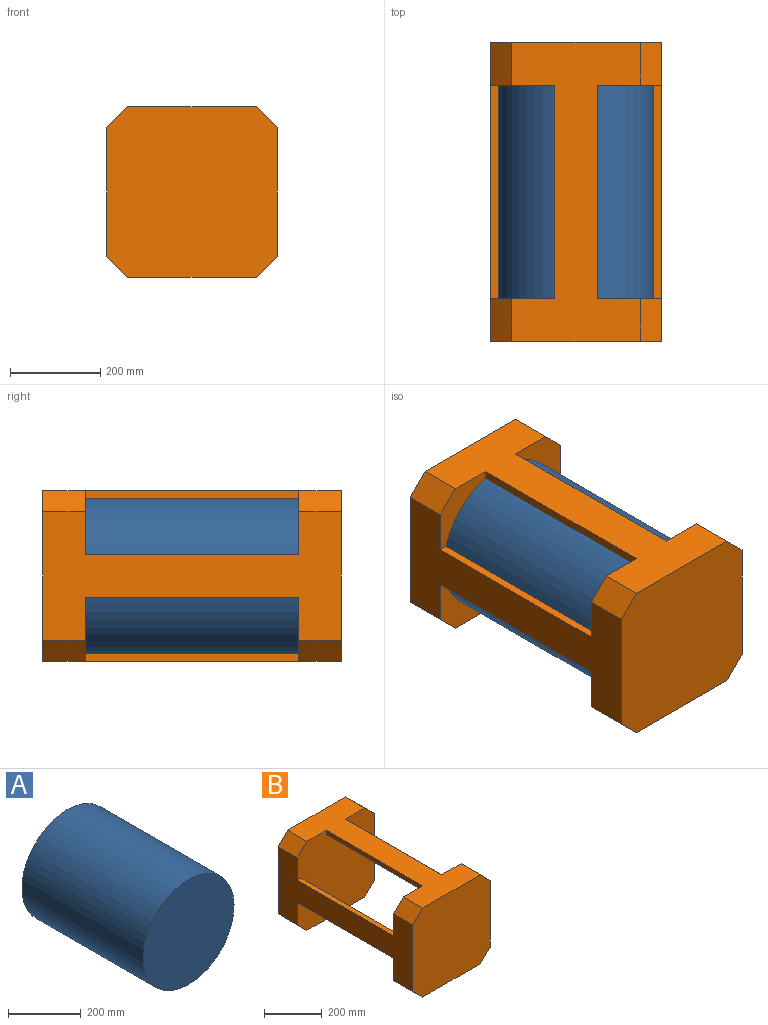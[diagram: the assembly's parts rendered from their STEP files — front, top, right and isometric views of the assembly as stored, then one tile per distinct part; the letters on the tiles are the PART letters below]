
ASSEMBLY  parts=2 mates=1
PART A: 3 faces, bbox 353.8x471.7x353.8 mm
  f0: cylinder r=176.89mm len=471.71mm, axis (0,-1,0), area 524287.1mm2, adj f1,f2
  f1: plane 353.79x353.79mm, normal (0,1,0), area 98303.8mm2, adj f0
  f2: plane 353.79x353.79mm, normal (0,-1,0), area 98303.8mm2, adj f0
PART B: 28 faces, bbox 377.4x660.4x377.4 mm
  f0: plane 377.37x377.37mm, normal (0,1,0), area 132708.8mm2, adj f1,f2,f3,f4,f5,f6,f7,f8
  f1: plane 660.4x283.03mm, normal (0,0,-1), area 97906.3mm2, adj f0,f2,f8,f9,f13,f14,f22,f23
  f2: plane 94.34x47.17mm, normal (0.71,0,-0.71), area 6293.7mm2, adj f0,f1,f3,f9
  f3: plane 660.4x283.03mm, normal (1,0,0), area 97906.3mm2, adj f0,f2,f4,f9,f19,f21,f22,f23
  f4: plane 94.34x47.17mm, normal (0.71,0,0.71), area 6293.7mm2, adj f0,f3,f5,f9
  f5: plane 660.4x283.03mm, normal (0,0,1), area 97906.3mm2, adj f0,f4,f6,f9,f10,f12,f22,f24
  f6: plane 94.34x47.17mm, normal (-0.71,0,0.71), area 6293.7mm2, adj f0,f5,f7,f9
  f7: plane 660.4x283.03mm, normal (-1,0,0), area 97906.3mm2, adj f0,f6,f8,f9,f17,f18,f22,f25
  f8: plane 94.34x47.17mm, normal (-0.71,0,-0.71), area 6293.7mm2, adj f0,f1,f7,f9
  f9: plane 377.37x377.37mm, normal (0,-1,0), area 137958.9mm2, adj f1,f2,f3,f4,f5,f6,f7,f8
  f10: plane 471.71x18.2mm, normal (-1,0,0), area 8584.4mm2, adj f0,f5,f11,f22
  f11: cylinder r=176.89mm len=471.71mm, axis (0,-1,0), area 45047.9mm2, adj f0,f10,f12,f22
  f12: plane 471.71x18.2mm, normal (1,0,0), area 8584.4mm2, adj f0,f5,f11,f22
  f13: plane 471.71x18.2mm, normal (-1,0,0), area 8584.4mm2, adj f0,f1,f15,f22
  f14: plane 471.71x18.2mm, normal (1,0,0), area 8584.4mm2, adj f0,f1,f15,f22
  f15: cylinder r=176.89mm len=471.71mm, axis (0,-1,0), area 45047.9mm2, adj f0,f13,f14,f22
  f16: cylinder r=176.89mm len=471.71mm, axis (0,-1,0), area 45047.9mm2, adj f0,f17,f18,f22
  f17: plane 471.71x18.2mm, normal (0,0,1), area 8584.4mm2, adj f0,f7,f16,f22
  f18: plane 471.71x18.2mm, normal (0,0,-1), area 8584.4mm2, adj f0,f7,f16,f22
  f19: plane 471.71x18.2mm, normal (0,0,1), area 8584.4mm2, adj f0,f3,f20,f22
  f20: cylinder r=176.89mm len=471.71mm, axis (0,-1,0), area 45047.9mm2, adj f0,f19,f21,f22
  f21: plane 471.71x18.2mm, normal (0,0,-1), area 8584.4mm2, adj f0,f3,f20,f22
  f22: plane 377.37x377.37mm, normal (0,-1,0), area 132708.8mm2, adj f1,f3,f5,f7,f10,f11,f12,f13
  f23: plane 94.34x47.17mm, normal (0.71,0,-0.71), area 6293.7mm2, adj f1,f3,f22,f27
  f24: plane 94.34x47.17mm, normal (0.71,0,0.71), area 6293.7mm2, adj f3,f5,f22,f27
  f25: plane 94.34x47.17mm, normal (-0.71,0,0.71), area 6293.7mm2, adj f5,f7,f22,f27
  f26: plane 94.34x47.17mm, normal (-0.71,0,-0.71), area 6293.7mm2, adj f1,f7,f22,f27
  f27: plane 377.37x377.37mm, normal (0,1,0), area 137958.9mm2, adj f1,f3,f5,f7,f23,f24,f25,f26
PLACE A t=(-526.6,-1016.21,2.59)mm
PLACE B t=(-3.36,-1016.21,2.59)mm
MATE fastened A.f0 <-> B.f20  axis (0,-1,0) through (-3.36,217.5,2.59)mm
